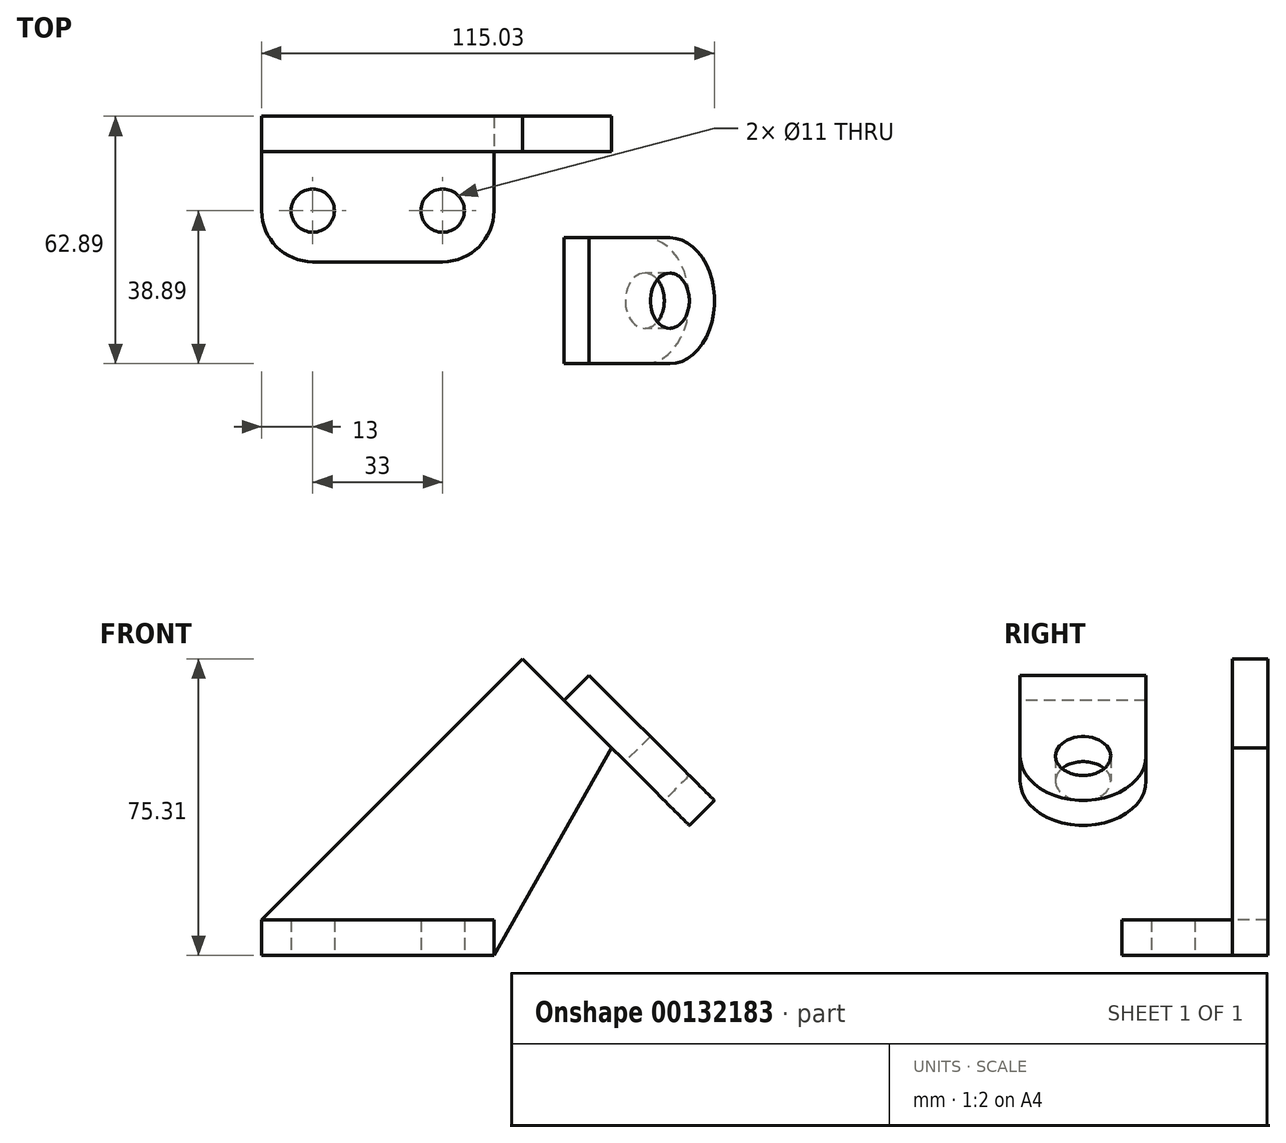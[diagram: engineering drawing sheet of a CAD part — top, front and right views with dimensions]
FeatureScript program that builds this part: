
annotation { "Feature Type Name" : "Feature", "Feature Type Description" : "" }
export const myFeature = defineFeature(function(context is Context, id is Id, definition is map)
    precondition{}
    {
        {
            var Q0;
            Q0=qCreatedBy(makeId("Top.planeOp"),FACE);
            var sketch = newSketch(context, id + "F0", { "sketchPlane" : qUnion([Q0])});
            skCircle(sketch, "E0", {"center": v(0, 0) * mm, "radius": 5.5 * mm});
            skCircle(sketch, "E1", {"center": v(-33, 0) * mm, "radius": 5.5 * mm});
            skArc(sketch, "E2", {"start": v(-46, 0) * mm, "mid": v(-42.2, -9.2) * mm, "end": v(-33, -13) * mm});
            skArc(sketch, "E3", {"start": v(13, 0) * mm, "mid": v(9.2, -9.2) * mm, "end": v(0, -13) * mm});
            skLineSegment(sketch, "E4", {"start": v(0, -13) * mm, "end": v(-33, -13) * mm});
            skLineSegment(sketch, "E5", {"start": v(13, 0) * mm, "end": v(13, 15) * mm});
            skLineSegment(sketch, "E6", {"start": v(13, 15) * mm, "end": v(-46, 15) * mm});
            skLineSegment(sketch, "E7", {"start": v(-46, 15) * mm, "end": v(-46, 0) * mm});
            skSolve(sketch);
        }
        {
            var Q0;
            Q0 = qSketchRegion(id + "F0", true);
            extrude(context, id + "F1", {"entities" : qUnion([Q0]), "depth" : 9 * mm});
        }
        {
            var Q0;
            Q0=makeQuery(id+"F1.opExtrude","SWEPT_FACE",FACE,{"disambiguationData":[OSD([sQuery(id+"F0.wireOp",EDGE,"E6")])]});
            var sketch = newSketch(context, id + "F2", { "sketchPlane" : qUnion([Q0])});
            skLineSegment(sketch, "E8", {"start": v(46, 9) * mm, "end": v(-20.31, 75.31) * mm});
            skLineSegment(sketch, "E9", {"start": v(-42.94, 52.69) * mm, "end": v(-20.31, 75.31) * mm});
            skPoint(sketch, "E10", {"position": v(-31.63, 64) * mm});
            skLineSegment(sketch, "E11", {"start": v(-31.63, 64) * mm, "end": v(-78.74, 64) * mm, "construction": true});
            skLineSegment(sketch, "E12", {"start": v(-42.94, 52.69) * mm, "end": v(-13, 0) * mm});
            skLineSegment(sketch, "E13", {"start": v(-13, 0) * mm, "end": v(46, 0) * mm});
            skLineSegment(sketch, "E14", {"start": v(46, 0) * mm, "end": v(46, 9) * mm});
            skSolve(sketch);
        }
        {
            var Q0;
            Q0 = qSketchRegion(id + "F2", true);
            extrude(context, id + "F3", {"entities" : qUnion([Q0]), "operationType" : NewBodyOperationType.ADD, "depth" : 9 * mm});
        }
        {
            var Q0;
            Q0=makeQuery(id+"F3.opExtrude","SWEPT_FACE",FACE,{"disambiguationData":[OSD([sQuery(id+"F2.wireOp",EDGE,"E9")])]});
            var sketch = newSketch(context, id + "F4", { "sketchPlane" : qUnion([Q0])});
            skCircle(sketch, "E15", {"center": v(-22.9, -5) * mm, "radius": 7 * mm});
            skLineSegment(sketch, "E16.0", {"start": v(-6.9, 24) * mm, "end": v(-38.9, 24) * mm});
            skLineSegment(sketch, "E17.0", {"start": v(-38.9, 24) * mm, "end": v(-38.9, 15) * mm});
            skLineSegment(sketch, "E18.0", {"start": v(-6.9, 24) * mm, "end": v(-6.9, 15) * mm});
            skArc(sketch, "E19", {"start": v(-38.9, -5) * mm, "mid": v(-22.9, -21) * mm, "end": v(-6.9, -5) * mm});
            skLineSegment(sketch, "E20", {"start": v(-38.9, -5) * mm, "end": v(-38.9, 15) * mm});
            skLineSegment(sketch, "E21", {"start": v(-6.9, 15) * mm, "end": v(-6.9, -5) * mm});
            skSolve(sketch);
        }
        {
            var Q0;
            Q0 = qSketchRegion(id + "F4", true);
            extrude(context, id + "F5", {"entities" : qUnion([Q0]), "operationType" : NewBodyOperationType.ADD, "depth" : 9 * mm});
        }
    });
